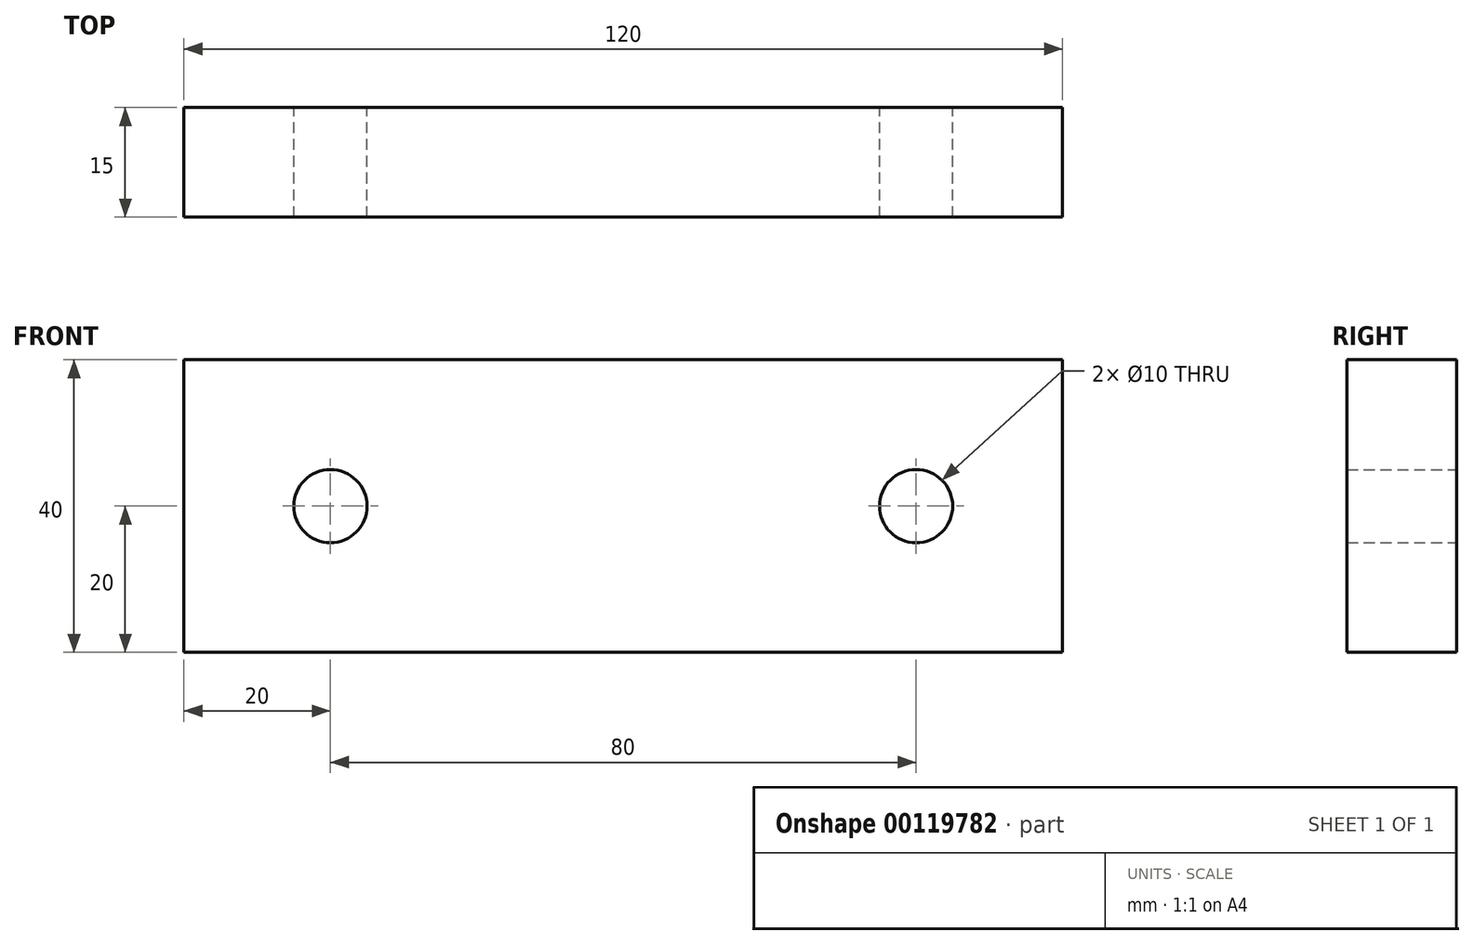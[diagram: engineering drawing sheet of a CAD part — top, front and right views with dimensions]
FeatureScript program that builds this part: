
annotation { "Feature Type Name" : "Feature", "Feature Type Description" : "" }
export const myFeature = defineFeature(function(context is Context, id is Id, definition is map)
    precondition{}
    {
        {
            var Q0;
            Q0=qCreatedBy(makeId("Front.planeOp"),FACE);
            var sketch = newSketch(context, id + "F0", { "sketchPlane" : qUnion([Q0])});
            skLineSegment(sketch, "E0.bottom", {"start": v(0, 0) * mm, "end": v(120, 0) * mm});
            skLineSegment(sketch, "E0.top", {"start": v(0, 40) * mm, "end": v(120, 40) * mm});
            skLineSegment(sketch, "E0.left", {"start": v(0, 0) * mm, "end": v(0, 40) * mm});
            skLineSegment(sketch, "E0.right", {"start": v(120, 0) * mm, "end": v(120, 40) * mm});
            skCircle(sketch, "E1", {"center": v(20, 20) * mm, "radius": 5 * mm});
            skPoint(sketch, "E1.centerSnap0", {"position": v(0, 20) * mm});
            skCircle(sketch, "E2", {"center": v(100, 20) * mm, "radius": 5 * mm});
            skPoint(sketch, "E2.centerSnap0", {"position": v(120, 20) * mm});
            skSolve(sketch);
        }
        {
            var Q0;
            Q0 = qSketchRegion(id + "F0", true);
            extrude(context, id + "F1", {"entities" : qUnion([Q0]), "endBound" : BoundingType.SYMMETRIC, "depth" : 15 * mm});
        }
    });
